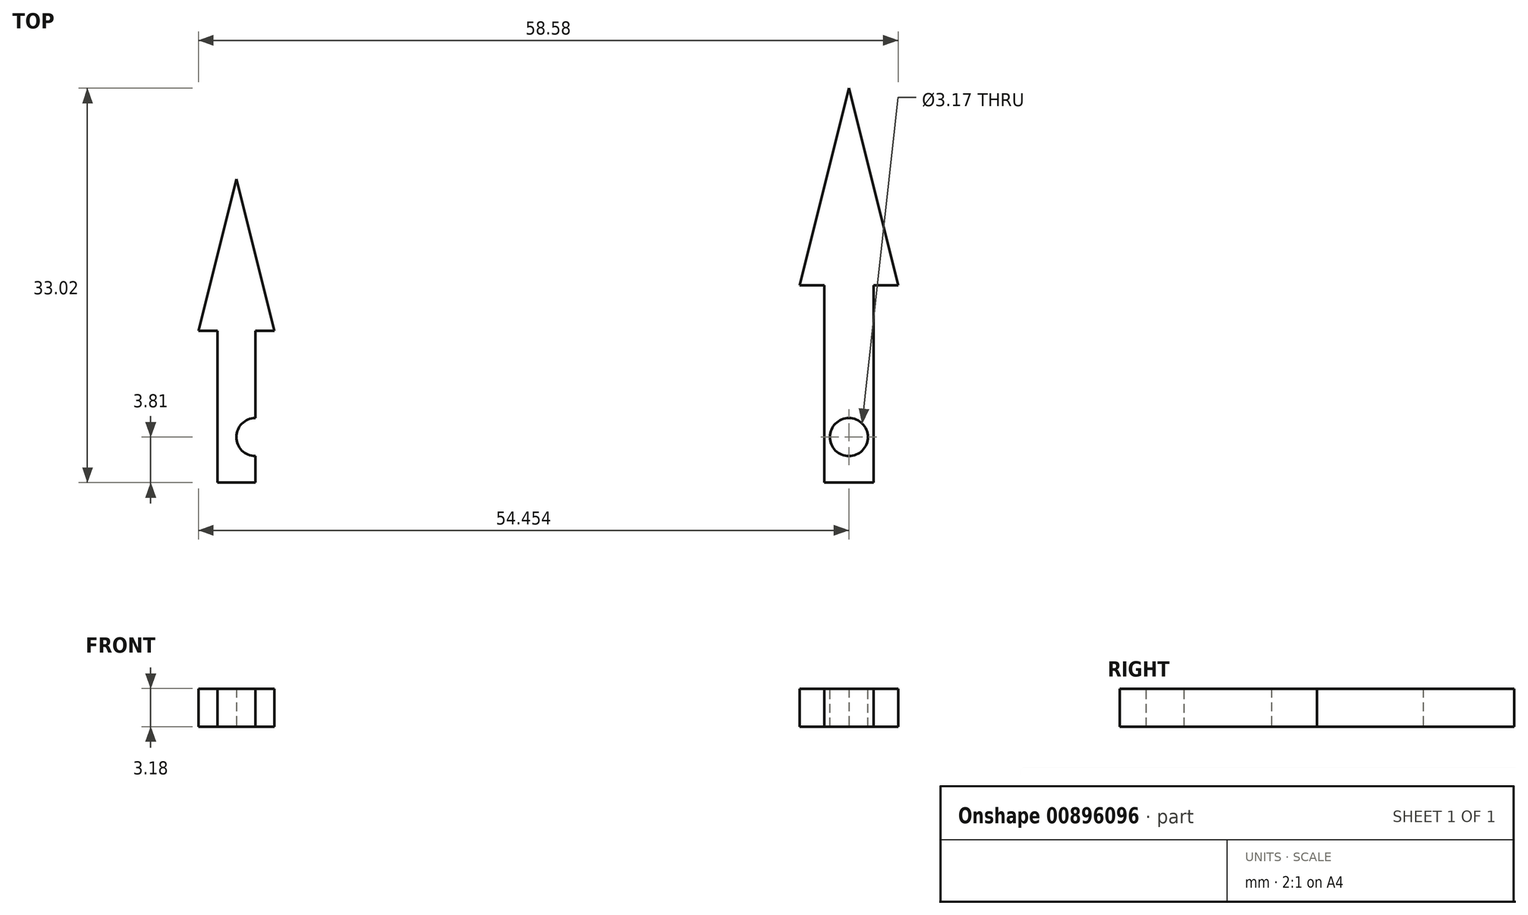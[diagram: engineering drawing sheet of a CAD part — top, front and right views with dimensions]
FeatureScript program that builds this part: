
annotation { "Feature Type Name" : "Feature", "Feature Type Description" : "" }
export const myFeature = defineFeature(function(context is Context, id is Id, definition is map)
    precondition{}
    {
        {
            var Q0;
            Q0=qCreatedBy(makeId("Top.planeOp"),FACE);
            var sketch = newSketch(context, id + "F0", { "sketchPlane" : qUnion([Q0])});
            skLineSegment(sketch, "E0.bottom", {"start": v(0, 0) * mm, "end": v(3.18, 0) * mm});
            skLineSegment(sketch, "E0.top", {"start": v(0, 12.7) * mm, "end": v(3.18, 12.7) * mm});
            skLineSegment(sketch, "E0.left", {"start": v(0, 0) * mm, "end": v(0, 12.7) * mm});
            skLineSegment(sketch, "E0.right", {"start": v(3.18, 0) * mm, "end": v(3.18, 12.7) * mm});
            skLineSegment(sketch, "E1", {"start": v(0, 12.7) * mm, "end": v(-1.59, 12.7) * mm});
            skLineSegment(sketch, "E2", {"start": v(-1.59, 12.7) * mm, "end": v(1.59, 25.4) * mm});
            skLineSegment(sketch, "E3", {"start": v(1.59, 25.4) * mm, "end": v(4.76, 12.7) * mm});
            skLineSegment(sketch, "E4", {"start": v(4.76, 12.7) * mm, "end": v(3.18, 12.7) * mm});
            skPoint(sketch, "E5", {"position": v(1.59, 0) * mm});
            skLineSegment(sketch, "E6", {"start": v(1.59, 0) * mm, "end": v(1.59, 25.18) * mm, "construction": true});
            skSolve(sketch);
        }
        {
            var Q0;
            Q0 = qSketchRegion(id + "F0", true);
            extrude(context, id + "F1", {"entities" : qUnion([Q0]), "depth" : 3.17 * mm, "offsetDistance" : 25.4 * mm});
        }
        {
            var Q0;
            Q0=makeQuery(id+"F1.opExtrude","CAP_FACE",FACE,{"disambiguationData":[OSD([sQuery(id+"F0.wireOp",EDGE,"E0.bottom"),sQuery(id+"F0.wireOp",EDGE,"E0.left"),sQuery(id+"F0.wireOp",EDGE,"E0.right"),sQuery(id+"F0.wireOp",EDGE,"E1"),sQuery(id+"F0.wireOp",EDGE,"E2"),sQuery(id+"F0.wireOp",EDGE,"E3"),sQuery(id+"F0.wireOp",EDGE,"E4")])],"isStart":false});
            var sketch = newSketch(context, id + "F2", { "sketchPlane" : qUnion([Q0])});
            skPoint(sketch, "E7", {"position": v(3.17, 3.81) * mm});
            skSolve(sketch);
        }
        {
            var Q0;
            Q0=makeQuery(id+"F1.opExtrude","SWEPT_BODY",BODY,{"disambiguationData":[OSD([sQuery(id+"F0.wireOp",EDGE,"E0.bottom"),sQuery(id+"F0.wireOp",EDGE,"E0.left"),sQuery(id+"F0.wireOp",EDGE,"E0.right"),sQuery(id+"F0.wireOp",EDGE,"E1"),sQuery(id+"F0.wireOp",EDGE,"E2"),sQuery(id+"F0.wireOp",EDGE,"E3"),sQuery(id+"F0.wireOp",EDGE,"E4")])]});
            transform(context, id + "F3", {"entities" : qUnion([Q0]), "transformType" : TransformType.TRANSLATION_3D, "dx" : 50.8 * mm, "dy" : 0 * mm, "dz" : 0 * mm, "makeCopy" : true});
        }
        {
            var Q0;
            Q0=makeQuery(id+"F3.opPattern","COPY",BODY,{"derivedFrom":makeQuery(id+"F1.opExtrude","SWEPT_BODY",BODY,{"disambiguationData":[OSD([sQuery(id+"F0.wireOp",EDGE,"E0.bottom"),sQuery(id+"F0.wireOp",EDGE,"E0.left"),sQuery(id+"F0.wireOp",EDGE,"E0.right"),sQuery(id+"F0.wireOp",EDGE,"E1"),sQuery(id+"F0.wireOp",EDGE,"E2"),sQuery(id+"F0.wireOp",EDGE,"E3"),sQuery(id+"F0.wireOp",EDGE,"E4")])]}),"instanceName":"1"});
            var Q1;
            Q1=makeQuery(id+"F3.opPattern","COPY",VERTEX,{"derivedFrom":makeQuery(id+"F1.opExtrude","CAP_VERTEX",VERTEX,{"disambiguationData":[OSD([sQuery(id+"F0.wireOp",EDGE,"E0.bottom"),sQuery(id+"F0.wireOp",EDGE,"E0.left")])],"isStart":false}),"instanceName":"1"});
            transform(context, id + "F4", {"entities" : qUnion([Q0]), "transformType" : TransformType.SCALE_UNIFORMLY, "scale" : 1.3, "scalePoint" : qUnion([Q1]), "makeCopy" : false});
        }
        {
            var Q0;
            Q0=makeQuery(id+"F3.opPattern","COPY",FACE,{"derivedFrom":makeQuery(id+"F1.opExtrude","CAP_FACE",FACE,{"disambiguationData":[OSD([sQuery(id+"F0.wireOp",EDGE,"E0.bottom"),sQuery(id+"F0.wireOp",EDGE,"E0.left"),sQuery(id+"F0.wireOp",EDGE,"E0.right"),sQuery(id+"F0.wireOp",EDGE,"E1"),sQuery(id+"F0.wireOp",EDGE,"E2"),sQuery(id+"F0.wireOp",EDGE,"E3"),sQuery(id+"F0.wireOp",EDGE,"E4")])],"isStart":false}),"instanceName":"1"});
            var sketch = newSketch(context, id + "F5", { "sketchPlane" : qUnion([Q0])});
            skLineSegment(sketch, "E8", {"start": v(52.86, 0) * mm, "end": v(52.86, 13.06) * mm, "construction": true});
            skPoint(sketch, "E9", {"position": v(52.86, 3.81) * mm});
            skSolve(sketch);
        }
        {
            var Q0;
            Q0=sQuery(id+"F5.wireOp",VERTEX,"E9");
            var Q1;
            Q1=makeQuery(id+"F3.opPattern","COPY",BODY,{"derivedFrom":makeQuery(id+"F1.opExtrude","SWEPT_BODY",BODY,{"disambiguationData":[OSD([sQuery(id+"F0.wireOp",EDGE,"E0.bottom"),sQuery(id+"F0.wireOp",EDGE,"E0.left"),sQuery(id+"F0.wireOp",EDGE,"E0.right"),sQuery(id+"F0.wireOp",EDGE,"E1"),sQuery(id+"F0.wireOp",EDGE,"E2"),sQuery(id+"F0.wireOp",EDGE,"E3"),sQuery(id+"F0.wireOp",EDGE,"E4")])]}),"instanceName":"1"});
            hole(context, id + "F6", {"style" : HoleStyle.SIMPLE, "endStyle" : HoleEndStyle.THROUGH, "holeDiameter" : 3.17 * mm, "majorDiameter" : 6.35 * mm, "isTappedThrough" : true, "tappedDepth" : 12.7 * mm, "tapClearance" : 3, "locations" : qUnion([Q0]), "scope" : qUnion([Q1])});
        }
        {
            var Q0;
            Q0=sQuery(id+"F2.wireOp",VERTEX,"E7");
            var Q1;
            Q1=makeQuery(id+"F1.opExtrude","SWEPT_BODY",BODY,{"disambiguationData":[OSD([sQuery(id+"F0.wireOp",EDGE,"E0.bottom"),sQuery(id+"F0.wireOp",EDGE,"E0.left"),sQuery(id+"F0.wireOp",EDGE,"E0.right"),sQuery(id+"F0.wireOp",EDGE,"E1"),sQuery(id+"F0.wireOp",EDGE,"E2"),sQuery(id+"F0.wireOp",EDGE,"E3"),sQuery(id+"F0.wireOp",EDGE,"E4")])]});
            hole(context, id + "F7", {"style" : HoleStyle.SIMPLE, "endStyle" : HoleEndStyle.THROUGH, "holeDiameter" : 3.17 * mm, "majorDiameter" : 6.35 * mm, "isTappedThrough" : true, "tappedDepth" : 12.7 * mm, "tapClearance" : 3, "locations" : qUnion([Q0]), "scope" : qUnion([Q1])});
        }
        {
            var Q0;
            Q0=makeQuery(id+"F3.opPattern","COPY",FACE,{"derivedFrom":makeQuery(id+"F1.opExtrude","CAP_FACE",FACE,{"disambiguationData":[OSD([sQuery(id+"F0.wireOp",EDGE,"E0.bottom"),sQuery(id+"F0.wireOp",EDGE,"E0.left"),sQuery(id+"F0.wireOp",EDGE,"E0.right"),sQuery(id+"F0.wireOp",EDGE,"E1"),sQuery(id+"F0.wireOp",EDGE,"E2"),sQuery(id+"F0.wireOp",EDGE,"E3"),sQuery(id+"F0.wireOp",EDGE,"E4")])],"isStart":true}),"instanceName":"1"});
            var Q1;
            Q1=makeQuery(id+"F1.opExtrude","CAP_FACE",FACE,{"disambiguationData":[OSD([sQuery(id+"F0.wireOp",EDGE,"E0.bottom"),sQuery(id+"F0.wireOp",EDGE,"E0.left"),sQuery(id+"F0.wireOp",EDGE,"E0.right"),sQuery(id+"F0.wireOp",EDGE,"E1"),sQuery(id+"F0.wireOp",EDGE,"E2"),sQuery(id+"F0.wireOp",EDGE,"E3"),sQuery(id+"F0.wireOp",EDGE,"E4")])],"isStart":true});
            extrude(context, id + "F8", {"entities" : qUnion([Q0]), "operationType" : NewBodyOperationType.REMOVE, "endBound" : BoundingType.UP_TO_SURFACE, "oppositeDirection" : true, "depth" : 25.4 * mm, "endBoundEntityFace" : qUnion([Q1]), "offsetDistance" : 25.4 * mm});
        }
    });
